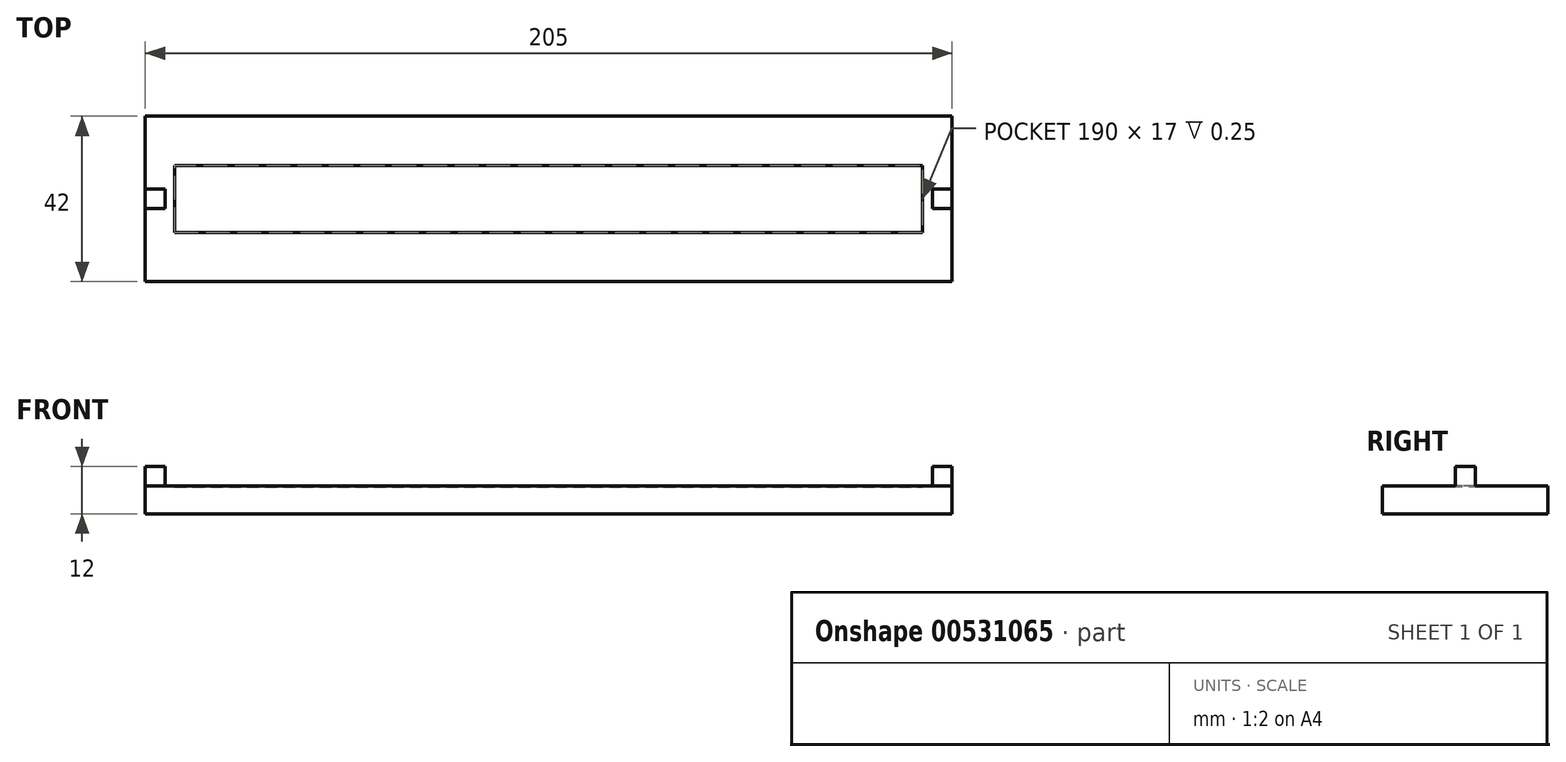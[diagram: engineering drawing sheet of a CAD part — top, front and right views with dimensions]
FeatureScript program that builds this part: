
annotation { "Feature Type Name" : "Feature", "Feature Type Description" : "" }
export const myFeature = defineFeature(function(context is Context, id is Id, definition is map)
    precondition{}
    {
        {
            var Q0;
            Q0=qCreatedBy(makeId("Top.planeOp"),FACE);
            var sketch = newSketch(context, id + "F0", { "sketchPlane" : qUnion([Q0])});
            skLineSegment(sketch, "E0.bottom", {"start": v(-102.5, -5.67) * mm, "end": v(102.5, -5.67) * mm});
            skLineSegment(sketch, "E0.top", {"start": v(-102.5, -47.67) * mm, "end": v(102.5, -47.67) * mm});
            skLineSegment(sketch, "E0.left", {"start": v(-102.5, -5.67) * mm, "end": v(-102.5, -47.67) * mm});
            skLineSegment(sketch, "E0.right", {"start": v(102.5, -5.67) * mm, "end": v(102.5, -47.67) * mm});
            skSolve(sketch);
        }
        {
            var Q0;
            Q0 = qSketchRegion(id + "F0", true);
            extrude(context, id + "F1", {"entities" : qUnion([Q0]), "depth" : 7 * mm, "offsetDistance" : 25 * mm});
        }
        {
            var Q0;
            Q0=makeQuery(id+"F1.opExtrude","CAP_FACE",FACE,{"disambiguationData":[OSD([sQuery(id+"F0.wireOp",EDGE,"E0.bottom"),sQuery(id+"F0.wireOp",EDGE,"E0.top"),sQuery(id+"F0.wireOp",EDGE,"E0.left"),sQuery(id+"F0.wireOp",EDGE,"E0.right")])],"isStart":false});
            var sketch = newSketch(context, id + "F2", { "sketchPlane" : qUnion([Q0])});
            skLineSegment(sketch, "E1", {"start": v(-102.5, -26.67) * mm, "end": v(102.5, -26.67) * mm, "construction": true});
            skLineSegment(sketch, "E2.bottom", {"start": v(-102.5, -24.17) * mm, "end": v(-97.5, -24.17) * mm});
            skLineSegment(sketch, "E2.top", {"start": v(-102.5, -29.17) * mm, "end": v(-97.5, -29.17) * mm});
            skLineSegment(sketch, "E2.left", {"start": v(-102.5, -24.17) * mm, "end": v(-102.5, -29.17) * mm});
            skLineSegment(sketch, "E2.right", {"start": v(-97.5, -24.17) * mm, "end": v(-97.5, -29.17) * mm});
            skLineSegment(sketch, "E3.MirrorCS", {"start": v(102.5, -24.17) * mm, "end": v(97.5, -24.17) * mm});
            skLineSegment(sketch, "E4.MirrorCS", {"start": v(102.5, -24.17) * mm, "end": v(102.5, -29.17) * mm});
            skLineSegment(sketch, "E5.MirrorCS", {"start": v(97.5, -24.17) * mm, "end": v(97.5, -29.17) * mm});
            skLineSegment(sketch, "E6.MirrorCS", {"start": v(102.5, -29.17) * mm, "end": v(97.5, -29.17) * mm});
            skLineSegment(sketch, "E7.bottom", {"start": v(-95, -18.17) * mm, "end": v(95, -18.17) * mm});
            skLineSegment(sketch, "E7.top", {"start": v(-95, -35.17) * mm, "end": v(95, -35.17) * mm});
            skLineSegment(sketch, "E7.left", {"start": v(-95, -18.17) * mm, "end": v(-95, -35.17) * mm});
            skLineSegment(sketch, "E7.right", {"start": v(95, -18.17) * mm, "end": v(95, -35.17) * mm});
            skSolve(sketch);
        }
        {
            var Q0;
            Q0=makeQuery(id+"F2.imprint","IMPRINT",FACE,{"disambiguationData":[TD([[makeQuery(id+"F2.imprint","IMPRINT",EDGE,{"derivedFrom":sQuery(id+"F2.wireOp",EDGE,"E2.bottom")}),-1.0]])]});
            var Q1;
            Q1=makeQuery(id+"F2.imprint","IMPRINT",FACE,{"disambiguationData":[TD([[makeQuery(id+"F2.imprint","IMPRINT",EDGE,{"derivedFrom":sQuery(id+"F2.wireOp",EDGE,"E3.MirrorCS")}),1.0]])]});
            extrude(context, id + "F3", {"entities" : qUnion([Q0, Q1]), "operationType" : NewBodyOperationType.ADD, "depth" : 5 * mm, "offsetDistance" : 25 * mm});
        }
        {
            var Q0;
            Q0=makeQuery(id+"F2.imprint","IMPRINT",FACE,{"disambiguationData":[TD([[makeQuery(id+"F2.imprint","IMPRINT",EDGE,{"derivedFrom":sQuery(id+"F2.wireOp",EDGE,"E7.bottom")}),-1.0]])]});
            extrude(context, id + "F4", {"entities" : qUnion([Q0]), "operationType" : NewBodyOperationType.REMOVE, "depth" : -.25 * mm, "offsetDistance" : 25 * mm});
        }
    });
